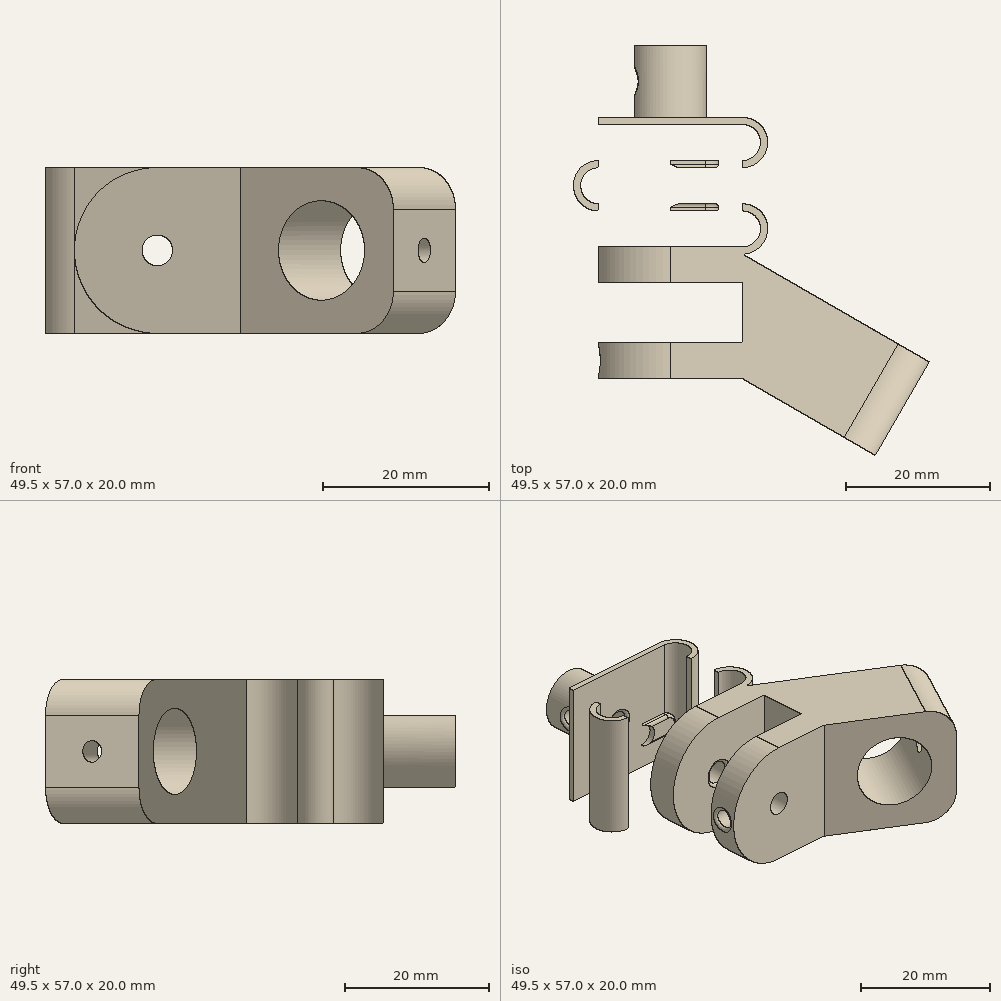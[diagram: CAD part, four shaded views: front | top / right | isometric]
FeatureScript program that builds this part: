
annotation { "Feature Type Name" : "Feature", "Feature Type Description" : "" }
export const myFeature = defineFeature(function(context is Context, id is Id, definition is map)
    precondition{}
    {
        {
            var Q0;
            Q0=qCreatedBy(makeId("Top.planeOp"),FACE);
            var sketch = newSketch(context, id + "F0", { "sketchPlane" : qUnion([Q0])});
            skLineSegment(sketch, "E0", {"start": v(0, 0) * mm, "end": v(25.98, -15) * mm});
            skLineSegment(sketch, "E1", {"start": v(25.98, -15) * mm, "end": v(18.48, -28) * mm});
            skLineSegment(sketch, "E2", {"start": v(18.48, -28) * mm, "end": v(0, -17.32) * mm});
            skLineSegment(sketch, "E3", {"start": v(0, -17.32) * mm, "end": v(0, 0) * mm});
            skLineSegment(sketch, "E4.bottom", {"start": v(0, -4) * mm, "end": v(-20, -4) * mm});
            skLineSegment(sketch, "E4.top", {"start": v(0, 1) * mm, "end": v(-20, 1) * mm});
            skLineSegment(sketch, "E4.left", {"start": v(0, -4) * mm, "end": v(0, 1) * mm});
            skLineSegment(sketch, "E4.right", {"start": v(-20, -4) * mm, "end": v(-20, 1) * mm});
            skLineSegment(sketch, "E5.bottom", {"start": v(0, 6) * mm, "end": v(-20, 6) * mm});
            skLineSegment(sketch, "E5.top", {"start": v(0, 7) * mm, "end": v(-20, 7) * mm});
            skLineSegment(sketch, "E5.left", {"start": v(0, 6) * mm, "end": v(0, 7) * mm});
            skLineSegment(sketch, "E5.right", {"start": v(-20, 6) * mm, "end": v(-20, 7) * mm});
            skLineSegment(sketch, "E6.bottom", {"start": v(0, 12) * mm, "end": v(-20, 12) * mm});
            skLineSegment(sketch, "E6.top", {"start": v(0, 13) * mm, "end": v(-20, 13) * mm});
            skLineSegment(sketch, "E6.left", {"start": v(0, 12) * mm, "end": v(0, 13) * mm});
            skLineSegment(sketch, "E6.right", {"start": v(-20, 12) * mm, "end": v(-20, 13) * mm});
            skLineSegment(sketch, "E7.bottom", {"start": v(0, 18) * mm, "end": v(-20, 18) * mm});
            skLineSegment(sketch, "E7.top", {"start": v(0, 19) * mm, "end": v(-20, 19) * mm});
            skLineSegment(sketch, "E7.left", {"start": v(0, 18) * mm, "end": v(0, 19) * mm});
            skLineSegment(sketch, "E7.right", {"start": v(-20, 18) * mm, "end": v(-20, 19) * mm});
            skLineSegment(sketch, "E8.bottom", {"start": v(0, -17.32) * mm, "end": v(-20, -17.32) * mm});
            skLineSegment(sketch, "E8.top", {"start": v(0, -12.32) * mm, "end": v(-20, -12.32) * mm});
            skLineSegment(sketch, "E8.left", {"start": v(0, -17.32) * mm, "end": v(0, -12.32) * mm});
            skLineSegment(sketch, "E8.right", {"start": v(-20, -17.32) * mm, "end": v(-20, -12.32) * mm});
            skArc(sketch, "E9", {"start": v(0, 6) * mm, "mid": v(2.5, 3.5) * mm, "end": v(0, 1) * mm});
            skArc(sketch, "E10", {"start": v(0, 7) * mm, "mid": v(3.5, 3.5) * mm, "end": v(0, 0) * mm});
            skArc(sketch, "E11", {"start": v(-20, 7) * mm, "mid": v(-22.5, 9.5) * mm, "end": v(-20, 12) * mm});
            skArc(sketch, "E12", {"start": v(-20, 13) * mm, "mid": v(-23.5, 9.5) * mm, "end": v(-20, 6) * mm});
            skArc(sketch, "E13", {"start": v(0, 18) * mm, "mid": v(2.5, 15.5) * mm, "end": v(0, 13) * mm});
            skArc(sketch, "E14", {"start": v(0, 19) * mm, "mid": v(3.5, 15.5) * mm, "end": v(0, 12) * mm});
            skSolve(sketch);
        }
        {
            var Q0;
            Q0 = qSketchRegion(id + "F0", true);
            extrude(context, id + "F1", {"entities" : qUnion([Q0]), "depth" : 20 * mm, "offsetDistance" : 25 * mm});
        }
        {
            var Q0;
            Q0=makeQuery(id+"F1.opExtrude","SWEPT_FACE",FACE,{"disambiguationData":[OSD([sQuery(id+"F0.wireOp",EDGE,"E0")])]});
            var sketch = newSketch(context, id + "F2", { "sketchPlane" : qUnion([Q0])});
            skCircle(sketch, "E15", {"center": v(-20, 10) * mm, "radius": 6 * mm});
            skLineSegment(sketch, "E16", {"start": v(-20, 10) * mm, "end": v(-20, 0) * mm, "construction": true});
            skLineSegment(sketch, "E17", {"start": v(-20, 10) * mm, "end": v(-30, 10) * mm, "construction": true});
            skSolve(sketch);
        }
        {
            var Q0;
            Q0=makeQuery(id+"F2.imprint","IMPRINT",FACE,{"disambiguationData":[TD([[makeQuery(id+"F2.imprint","IMPRINT",EDGE,{"derivedFrom":sQuery(id+"F2.wireOp",EDGE,"E15")}),1.0]])]});
            var Q1;
            Q1=makeQuery(id+"F1.opExtrude","SWEPT_FACE",FACE,{"disambiguationData":[OSD([sQuery(id+"F0.wireOp",EDGE,"E2")])]});
            extrude(context, id + "F3", {"entities" : qUnion([Q0]), "operationType" : NewBodyOperationType.REMOVE, "endBound" : BoundingType.UP_TO_SURFACE, "oppositeDirection" : true, "depth" : 25 * mm, "endBoundEntityFace" : qUnion([Q1]), "offsetDistance" : 25 * mm});
        }
        {
            var Q0;
            Q0=makeQuery(id+"F1.opExtrude","SWEPT_FACE",FACE,{"disambiguationData":[OSD([sQuery(id+"F0.wireOp",EDGE,"E1")])]});
            var sketch = newSketch(context, id + "F4", { "sketchPlane" : qUnion([Q0])});
            skCircle(sketch, "E18", {"center": v(-7.5, 10) * mm, "radius": 1.5 * mm});
            skPoint(sketch, "E19", {"position": v(0, 10) * mm});
            skPoint(sketch, "E20", {"position": v(-7.5, 0) * mm});
            skSolve(sketch);
        }
        {
            var Q0;
            Q0=makeQuery(id+"F4.imprint","IMPRINT",FACE,{"disambiguationData":[TD([[makeQuery(id+"F4.imprint","IMPRINT",EDGE,{"derivedFrom":sQuery(id+"F4.wireOp",EDGE,"E18")}),1.0]])]});
            var Q1;
            Q1=makeQuery(id+"F3.boolean.opBoolean","COPY",FACE,{"derivedFrom":makeQuery(id+"F3.opExtrude","SWEPT_FACE",FACE,{"disambiguationData":[OSD([sQuery(id+"F2.wireOp",EDGE,"E15")])]})});
            extrude(context, id + "F5", {"entities" : qUnion([Q0]), "operationType" : NewBodyOperationType.REMOVE, "endBound" : BoundingType.UP_TO_SURFACE, "oppositeDirection" : true, "depth" : 25 * mm, "endBoundEntityFace" : qUnion([Q1]), "offsetDistance" : 25 * mm});
        }
        {
            var Q0;
            Q0=makeQuery(id+"F1.opExtrude","SWEPT_FACE",FACE,{"disambiguationData":[OSD([sQuery(id+"F0.wireOp",EDGE,"E8.bottom")])]});
            var sketch = newSketch(context, id + "F6", { "sketchPlane" : qUnion([Q0])});
            skCircle(sketch, "E21", {"center": v(-10, 10) * mm, "radius": 1.85 * mm});
            skPoint(sketch, "E22", {"position": v(-20, 10) * mm});
            skPoint(sketch, "E23", {"position": v(-10, 0) * mm});
            skSolve(sketch);
        }
        {
            var Q0;
            Q0=makeQuery(id+"F1.opExtrude","SWEPT_FACE",FACE,{"disambiguationData":[OSD([sQuery(id+"F0.wireOp",EDGE,"E7.top")])]});
            var sketch = newSketch(context, id + "F7", { "sketchPlane" : qUnion([Q0])});
            skLineSegment(sketch, "E24.bottom", {"start": v(15, 5) * mm, "end": v(5, 5) * mm});
            skLineSegment(sketch, "E24.top", {"start": v(15, 15) * mm, "end": v(5, 15) * mm});
            skLineSegment(sketch, "E24.left", {"start": v(15, 5) * mm, "end": v(15, 15) * mm});
            skLineSegment(sketch, "E24.right", {"start": v(5, 5) * mm, "end": v(5, 15) * mm});
            skPoint(sketch, "E25", {"position": v(15, 10) * mm});
            skPoint(sketch, "E26", {"position": v(10, 5) * mm});
            skSolve(sketch);
        }
        {
            var Q0;
            Q0=makeQuery(id+"F7.imprint","IMPRINT",FACE,{"disambiguationData":[TD([[makeQuery(id+"F7.imprint","IMPRINT",EDGE,{"derivedFrom":sQuery(id+"F7.wireOp",EDGE,"E24.bottom")}),-1.0]])]});
            extrude(context, id + "F8", {"entities" : qUnion([Q0]), "operationType" : NewBodyOperationType.ADD, "depth" : 10 * mm, "offsetDistance" : 25 * mm});
        }
        {
            var Q0;
            Q0=makeQuery(id+"F6.imprint","IMPRINT",FACE,{"disambiguationData":[TD([[makeQuery(id+"F6.imprint","IMPRINT",EDGE,{"derivedFrom":sQuery(id+"F6.wireOp",EDGE,"E21")}),1.0]])]});
            var Q1;
            Q1=makeQuery(id+"F8.opExtrude","CAP_FACE",FACE,{"disambiguationData":[OSD([sQuery(id+"F7.wireOp",EDGE,"E24.bottom"),sQuery(id+"F7.wireOp",EDGE,"E24.top"),sQuery(id+"F7.wireOp",EDGE,"E24.left"),sQuery(id+"F7.wireOp",EDGE,"E24.right")])],"isStart":false});
            extrude(context, id + "F9", {"entities" : qUnion([Q0]), "operationType" : NewBodyOperationType.REMOVE, "endBound" : BoundingType.UP_TO_SURFACE, "oppositeDirection" : true, "depth" : 25 * mm, "endBoundEntityFace" : qUnion([Q1]), "offsetDistance" : 25 * mm});
        }
        {
            var Q0;
            Q0=makeQuery(id+"F1.opExtrude","SWEPT_FACE",FACE,{"disambiguationData":[OSD([sQuery(id+"F0.wireOp",EDGE,"E8.right")])]});
            var sketch = newSketch(context, id + "F10", { "sketchPlane" : qUnion([Q0])});
            skCircle(sketch, "E27", {"center": v(14.82, 10) * mm, "radius": 1.5 * mm});
            skPoint(sketch, "E28", {"position": v(14.82, 20) * mm});
            skPoint(sketch, "E29", {"position": v(12.32, 10) * mm});
            skSolve(sketch);
        }
        {
            var Q0;
            Q0=makeQuery(id+"F10.imprint","IMPRINT",FACE,{"disambiguationData":[TD([[makeQuery(id+"F10.imprint","IMPRINT",EDGE,{"derivedFrom":sQuery(id+"F10.wireOp",EDGE,"E27")}),1.0]])]});
            var Q1;
            Q1=sQuery(id+"F10.wireOp",EDGE,"E27");
            var Q2;
            Q2=makeQuery(id+"F9.boolean.opBoolean","COPY",FACE,{"disambiguationData":[TD([makeQuery(id+"F1.opExtrude","SWEPT_FACE",FACE,{"disambiguationData":[OSD([sQuery(id+"F0.wireOp",EDGE,"E8.bottom")])]})])],"derivedFrom":makeQuery(id+"F9.opExtrude","SWEPT_FACE",FACE,{"disambiguationData":[OSD([sQuery(id+"F6.wireOp",EDGE,"E21")])]})});
            extrude(context, id + "F11", {"entities" : qUnion([Q0]), "operationType" : NewBodyOperationType.REMOVE, "surfaceEntities" : qUnion([Q1]), "endBound" : BoundingType.UP_TO_SURFACE, "oppositeDirection" : true, "depth" : 25 * mm, "endBoundEntityFace" : qUnion([Q2]), "offsetDistance" : 25 * mm});
        }
        {
            var Q0;
            Q0=makeQuery(id+"F8.opExtrude","SWEPT_FACE",FACE,{"disambiguationData":[OSD([sQuery(id+"F7.wireOp",EDGE,"E24.left")])]});
            var sketch = newSketch(context, id + "F12", { "sketchPlane" : qUnion([Q0])});
            skCircle(sketch, "E30", {"center": v(-24, 10) * mm, "radius": 1.5 * mm});
            skPoint(sketch, "E31", {"position": v(-24, 15) * mm});
            skPoint(sketch, "E32", {"position": v(-29, 10) * mm});
            skSolve(sketch);
        }
        {
            var Q0;
            Q0=makeQuery(id+"F12.imprint","IMPRINT",FACE,{"disambiguationData":[TD([[makeQuery(id+"F12.imprint","IMPRINT",EDGE,{"derivedFrom":sQuery(id+"F12.wireOp",EDGE,"E30")}),1.0]])]});
            var Q1;
            Q1=makeQuery(id+"F9.boolean.opBoolean","COPY",FACE,{"disambiguationData":[TD([makeQuery(id+"F1.opExtrude","SWEPT_FACE",FACE,{"disambiguationData":[OSD([sQuery(id+"F0.wireOp",EDGE,"E7.bottom")])]})])],"derivedFrom":makeQuery(id+"F9.opExtrude","SWEPT_FACE",FACE,{"disambiguationData":[OSD([sQuery(id+"F6.wireOp",EDGE,"E21")])]})});
            extrude(context, id + "F13", {"entities" : qUnion([Q0]), "operationType" : NewBodyOperationType.REMOVE, "endBound" : BoundingType.UP_TO_SURFACE, "oppositeDirection" : true, "depth" : 25 * mm, "endBoundEntityFace" : qUnion([Q1]), "offsetDistance" : 25 * mm});
        }
        {
            var Q0;
            Q0=makeQuery(id+"F1.opExtrude","SWEPT_FACE",FACE,{"disambiguationData":[OSD([sQuery(id+"F0.wireOp",EDGE,"E5.top")])]});
            var sketch = newSketch(context, id + "F14", { "sketchPlane" : qUnion([Q0])});
            skLineSegment(sketch, "E33.bottom", {"start": v(14.85, 8.15) * mm, "end": v(5.15, 8.15) * mm});
            skLineSegment(sketch, "E33.top", {"start": v(14.85, 11.85) * mm, "end": v(5.15, 11.85) * mm});
            skLineSegment(sketch, "E33.left", {"start": v(14.85, 8.15) * mm, "end": v(14.85, 11.85) * mm, "construction": true});
            skLineSegment(sketch, "E33.right", {"start": v(5.15, 8.15) * mm, "end": v(5.15, 11.85) * mm, "construction": true});
            skPoint(sketch, "E34", {"position": v(10, 11.85) * mm});
            skArc(sketch, "E35", {"start": v(5.15, 8.15) * mm, "mid": v(3.3, 10) * mm, "end": v(5.15, 11.85) * mm});
            skArc(sketch, "E36", {"start": v(14.85, 8.15) * mm, "mid": v(16.7, 10) * mm, "end": v(14.85, 11.85) * mm});
            skSolve(sketch);
        }
        {
            var Q0;
            {var subQ0=sQuery(id+"F14.wireOp",EDGE,"E35");Q0=makeQuery(id+"F14.imprint","IMPRINT",FACE,{"disambiguationData":[TD([[makeQuery(id+"F14.imprint","IMPRINT",EDGE,{"derivedFrom":subQ0}),-1.0]])]});}
            var Q1;
            {var subQ0=sQuery(id+"F14.wireOp",EDGE,"E36");Q1=makeQuery(id+"F14.imprint","IMPRINT",FACE,{"disambiguationData":[TD([[makeQuery(id+"F14.imprint","IMPRINT",EDGE,{"derivedFrom":subQ0}),1.0]])]});}
            var Q2;
            Q2=makeQuery(id+"F1.opExtrude","SWEPT_FACE",FACE,{"disambiguationData":[OSD([sQuery(id+"F0.wireOp",EDGE,"E5.bottom")])]});
            var Q3;
            Q3=makeQuery(id+"F1.opExtrude","SWEPT_FACE",FACE,{"disambiguationData":[OSD([sQuery(id+"F0.wireOp",EDGE,"E6.top")])]});
            extrude(context, id + "F15", {"entities" : qUnion([Q0, Q1]), "operationType" : NewBodyOperationType.REMOVE, "endBound" : BoundingType.UP_TO_SURFACE, "oppositeDirection" : true, "depth" : 4 * mm, "endBoundEntityFace" : qUnion([Q2]), "offsetDistance" : 25 * mm, "hasSecondDirection" : true, "secondDirectionBound" : SecondDirectionBoundingType.UP_TO_SURFACE, "secondDirectionOppositeDirection" : false, "secondDirectionDepth" : 25 * mm, "secondDirectionBoundEntityFace" : qUnion([Q3])});
        }
        {
            var Q0;
            Q0=makeQuery(id+"F1.opExtrude","CAP_EDGE",EDGE,{"disambiguationData":[OSD([sQuery(id+"F0.wireOp",EDGE,"E1")])],"isStart":false});
            var Q1;
            Q1=makeQuery(id+"F1.opExtrude","CAP_EDGE",EDGE,{"disambiguationData":[OSD([sQuery(id+"F0.wireOp",EDGE,"E1")])],"isStart":true});
            var Q2;
            Q2=makeQuery(id+"F8.opExtrude","SWEPT_EDGE",EDGE,{"disambiguationData":[OSD([sQuery(id+"F7.wireOp",EDGE,"E24.top"),sQuery(id+"F7.wireOp",EDGE,"E24.left")])]});
            var Q3;
            Q3=makeQuery(id+"F8.opExtrude","SWEPT_EDGE",EDGE,{"disambiguationData":[OSD([sQuery(id+"F7.wireOp",EDGE,"E24.top"),sQuery(id+"F7.wireOp",EDGE,"E24.right")])]});
            var Q4;
            Q4=makeQuery(id+"F8.opExtrude","SWEPT_EDGE",EDGE,{"disambiguationData":[OSD([sQuery(id+"F7.wireOp",EDGE,"E24.bottom"),sQuery(id+"F7.wireOp",EDGE,"E24.right")])]});
            var Q5;
            Q5=makeQuery(id+"F8.opExtrude","SWEPT_EDGE",EDGE,{"disambiguationData":[OSD([sQuery(id+"F7.wireOp",EDGE,"E24.bottom"),sQuery(id+"F7.wireOp",EDGE,"E24.left")])]});
            fillet(context, id + "F16", {"entities" : qUnion([Q0, Q1, Q2, Q3, Q4, Q5]), "radius" : 5 * mm, "tangentPropagation" : true, "allowEdgeOverflow" : false});
        }
        {
            var Q0;
            Q0=makeQuery(id+"F1.opExtrude","CAP_EDGE",EDGE,{"disambiguationData":[OSD([sQuery(id+"F0.wireOp",EDGE,"E8.right")])],"isStart":false});
            var Q1;
            Q1=makeQuery(id+"F1.opExtrude","CAP_EDGE",EDGE,{"disambiguationData":[OSD([sQuery(id+"F0.wireOp",EDGE,"E8.right")])],"isStart":true});
            var Q2;
            Q2=makeQuery(id+"F1.opExtrude","CAP_EDGE",EDGE,{"disambiguationData":[OSD([sQuery(id+"F0.wireOp",EDGE,"E4.right")])],"isStart":false});
            var Q3;
            Q3=makeQuery(id+"F1.opExtrude","CAP_EDGE",EDGE,{"disambiguationData":[OSD([sQuery(id+"F0.wireOp",EDGE,"E4.right")])],"isStart":true});
            fillet(context, id + "F17", {"entities" : qUnion([Q0, Q1, Q2, Q3]), "radius" : 10 * mm, "tangentPropagation" : true, "allowEdgeOverflow" : false});
        }
        {
            var Q0;
            Q0=makeQuery(id+"F5.boolean.opBoolean","COPY",EDGE,{"derivedFrom":makeQuery(id+"F5.opExtrude","CAP_EDGE",EDGE,{"disambiguationData":[OSD([sQuery(id+"F4.wireOp",EDGE,"E18")])],"isStart":true})});
            var Q1;
            Q1=makeQuery(id+"F9.boolean.opBoolean","COPY",EDGE,{"derivedFrom":makeQuery(id+"F9.opExtrude","TWEAK_EDGE",EDGE,{"derivedFrom":[makeQuery(id+"F6.imprint","IMPRINT",EDGE,{"derivedFrom":sQuery(id+"F6.wireOp",EDGE,"E21")}),makeQuery(id+"F8.opExtrude","CAP_FACE",FACE,{"disambiguationData":[OSD([sQuery(id+"F7.wireOp",EDGE,"E24.bottom"),sQuery(id+"F7.wireOp",EDGE,"E24.top"),sQuery(id+"F7.wireOp",EDGE,"E24.left"),sQuery(id+"F7.wireOp",EDGE,"E24.right")])],"isStart":false})]})});
            var Q2;
            Q2=makeQuery(id+"F13.boolean.opBoolean","COPY",EDGE,{"derivedFrom":makeQuery(id+"F13.opExtrude","CAP_EDGE",EDGE,{"disambiguationData":[OSD([sQuery(id+"F12.wireOp",EDGE,"E30")])],"isStart":true})});
            var Q3;
            Q3=makeQuery(id+"F9.boolean.opBoolean","COPY",EDGE,{"derivedFrom":makeQuery(id+"F9.opExtrude","CAP_EDGE",EDGE,{"disambiguationData":[OSD([sQuery(id+"F6.wireOp",EDGE,"E21")])],"isStart":true})});
            var Q4;
            Q4=makeQuery(id+"F9.boolean.opBoolean","INTERSECT",EDGE,{"derivedFrom":[makeQuery(id+"F1.opExtrude","SWEPT_FACE",FACE,{"disambiguationData":[OSD([sQuery(id+"F0.wireOp",EDGE,"E4.bottom")])]}),makeQuery(id+"F9.opExtrude","SWEPT_FACE",FACE,{"disambiguationData":[OSD([sQuery(id+"F6.wireOp",EDGE,"E21")])]})]});
            var Q5;
            Q5=makeQuery(id+"F9.boolean.opBoolean","INTERSECT",EDGE,{"derivedFrom":[makeQuery(id+"F1.opExtrude","SWEPT_FACE",FACE,{"disambiguationData":[OSD([sQuery(id+"F0.wireOp",EDGE,"E8.top")])]}),makeQuery(id+"F9.opExtrude","SWEPT_FACE",FACE,{"disambiguationData":[OSD([sQuery(id+"F6.wireOp",EDGE,"E21")])]})]});
            var Q6;
            Q6=makeQuery(id+"F9.boolean.opBoolean","INTERSECT",EDGE,{"derivedFrom":[makeQuery(id+"F1.opExtrude","SWEPT_FACE",FACE,{"disambiguationData":[OSD([sQuery(id+"F0.wireOp",EDGE,"E4.top")])]}),makeQuery(id+"F9.opExtrude","SWEPT_FACE",FACE,{"disambiguationData":[OSD([sQuery(id+"F6.wireOp",EDGE,"E21")])]})]});
            var Q7;
            Q7=makeQuery(id+"F9.boolean.opBoolean","INTERSECT",EDGE,{"derivedFrom":[makeQuery(id+"F1.opExtrude","SWEPT_FACE",FACE,{"disambiguationData":[OSD([sQuery(id+"F0.wireOp",EDGE,"E7.bottom")])]}),makeQuery(id+"F9.opExtrude","SWEPT_FACE",FACE,{"disambiguationData":[OSD([sQuery(id+"F6.wireOp",EDGE,"E21")])]})]});
            var Q8;
            Q8=makeQuery(id+"F3.boolean.opBoolean","COPY",EDGE,{"derivedFrom":makeQuery(id+"F3.opExtrude","CAP_EDGE",EDGE,{"disambiguationData":[OSD([sQuery(id+"F2.wireOp",EDGE,"E15")])],"isStart":true})});
            var Q9;
            Q9=makeQuery(id+"F3.boolean.opBoolean","COPY",EDGE,{"derivedFrom":makeQuery(id+"F3.opExtrude","TWEAK_EDGE",EDGE,{"derivedFrom":[makeQuery(id+"F1.opExtrude","SWEPT_FACE",FACE,{"disambiguationData":[OSD([sQuery(id+"F0.wireOp",EDGE,"E2")])]}),makeQuery(id+"F2.imprint","IMPRINT",EDGE,{"derivedFrom":sQuery(id+"F2.wireOp",EDGE,"E15")})]})});
            var Q10;
            {var subQ0=sQuery(id+"F14.wireOp",EDGE,"E33.top");var subQ1=makeQuery(id+"F1.opExtrude","SWEPT_FACE",FACE,{"disambiguationData":[OSD([sQuery(id+"F0.wireOp",EDGE,"E5.top")])]});Q10=makeQuery(id+"F15.boolean.opBoolean","INTERSECT",EDGE,{"derivedFrom":[subQ1,makeQuery(id+"F15.opExtrude","SWEPT_FACE",FACE,{"disambiguationData":[OSD([subQ0]),TDD([makeQuery(id+"F14.imprint","IMPRINT",EDGE,{"disambiguationData":[TD([[makeQuery(id+"F14.imprint","INTERSECT",VERTEX,{"derivedFrom":[subQ0,sQuery(id+"F14.wireOp",EDGE,"E36")]}),-1.0]])],"derivedFrom":subQ0})])]}),makeQuery(id+"F15.opExtrude","SWEPT_FACE",FACE,{"disambiguationData":[OSD([subQ0]),TDD([makeQuery(id+"F14.imprint","IMPRINT",EDGE,{"disambiguationData":[TD([[makeQuery(id+"F14.imprint","INTERSECT",VERTEX,{"derivedFrom":[subQ0,sQuery(id+"F14.wireOp",EDGE,"E35")]}),1.0]])],"derivedFrom":subQ0})])]})]});}
            var Q11;
            {var subQ0=sQuery(id+"F14.wireOp",EDGE,"E33.top");var subQ2=makeQuery(id+"F1.opExtrude","SWEPT_FACE",FACE,{"disambiguationData":[OSD([sQuery(id+"F0.wireOp",EDGE,"E6.top")])]});Q11=makeQuery(id+"F15.boolean.opBoolean","TWEAK_EDGE",EDGE,{"derivedFrom":[makeQuery(id+"F15.opExtrude","TWEAK_EDGE",EDGE,{"derivedFrom":[subQ2,makeQuery(id+"F14.imprint","IMPRINT",EDGE,{"disambiguationData":[TD([[makeQuery(id+"F14.imprint","INTERSECT",VERTEX,{"derivedFrom":[subQ0,sQuery(id+"F14.wireOp",EDGE,"E36")]}),-1.0]])],"derivedFrom":subQ0})]}),makeQuery(id+"F15.opExtrude","TWEAK_EDGE",EDGE,{"derivedFrom":[subQ2,makeQuery(id+"F14.imprint","IMPRINT",EDGE,{"disambiguationData":[TD([[makeQuery(id+"F14.imprint","INTERSECT",VERTEX,{"derivedFrom":[subQ0,sQuery(id+"F14.wireOp",EDGE,"E35")]}),1.0]])],"derivedFrom":subQ0})]})]});}
            var Q12;
            {var subQ0=sQuery(id+"F14.wireOp",EDGE,"E33.top");Q12=makeQuery(id+"F15.boolean.opBoolean","INTERSECT",EDGE,{"derivedFrom":[makeQuery(id+"F1.opExtrude","SWEPT_FACE",FACE,{"disambiguationData":[OSD([sQuery(id+"F0.wireOp",EDGE,"E6.bottom")])]}),makeQuery(id+"F15.opExtrude","SWEPT_FACE",FACE,{"disambiguationData":[OSD([subQ0]),TDD([makeQuery(id+"F14.imprint","IMPRINT",EDGE,{"disambiguationData":[TD([[makeQuery(id+"F14.imprint","INTERSECT",VERTEX,{"derivedFrom":[subQ0,sQuery(id+"F14.wireOp",EDGE,"E36")]}),-1.0]])],"derivedFrom":subQ0})])]}),makeQuery(id+"F15.opExtrude","SWEPT_FACE",FACE,{"disambiguationData":[OSD([subQ0]),TDD([makeQuery(id+"F14.imprint","IMPRINT",EDGE,{"disambiguationData":[TD([[makeQuery(id+"F14.imprint","INTERSECT",VERTEX,{"derivedFrom":[subQ0,sQuery(id+"F14.wireOp",EDGE,"E35")]}),1.0]])],"derivedFrom":subQ0})])]})]});}
            var Q13;
            {var subQ0=sQuery(id+"F14.wireOp",EDGE,"E33.top");var subQ2=makeQuery(id+"F1.opExtrude","SWEPT_FACE",FACE,{"disambiguationData":[OSD([sQuery(id+"F0.wireOp",EDGE,"E5.bottom")])]});Q13=makeQuery(id+"F15.boolean.opBoolean","TWEAK_EDGE",EDGE,{"derivedFrom":[makeQuery(id+"F15.opExtrude","TWEAK_EDGE",EDGE,{"derivedFrom":[subQ2,makeQuery(id+"F14.imprint","IMPRINT",EDGE,{"disambiguationData":[TD([[makeQuery(id+"F14.imprint","INTERSECT",VERTEX,{"derivedFrom":[subQ0,sQuery(id+"F14.wireOp",EDGE,"E36")]}),-1.0]])],"derivedFrom":subQ0})]}),makeQuery(id+"F15.opExtrude","TWEAK_EDGE",EDGE,{"derivedFrom":[subQ2,makeQuery(id+"F14.imprint","IMPRINT",EDGE,{"disambiguationData":[TD([[makeQuery(id+"F14.imprint","INTERSECT",VERTEX,{"derivedFrom":[subQ0,sQuery(id+"F14.wireOp",EDGE,"E35")]}),1.0]])],"derivedFrom":subQ0})]})]});}
            var Q14;
            Q14=makeQuery(id+"F16.opFillet","BLEND_EDGE",EDGE,{"blendedFrom":[makeQuery(id+"F8.opExtrude","SWEPT_EDGE",EDGE,{"disambiguationData":[OSD([sQuery(id+"F7.wireOp",EDGE,"E24.bottom"),sQuery(id+"F7.wireOp",EDGE,"E24.right")])]}),makeQuery(id+"F13.boolean.opBoolean","COPY",FACE,{"derivedFrom":makeQuery(id+"F13.opExtrude","SWEPT_FACE",FACE,{"disambiguationData":[OSD([sQuery(id+"F12.wireOp",EDGE,"E30")])]})})],"blendedInto":[makeQuery(id+"F13.boolean.opBoolean","COPY",FACE,{"derivedFrom":makeQuery(id+"F13.opExtrude","SWEPT_FACE",FACE,{"disambiguationData":[OSD([sQuery(id+"F12.wireOp",EDGE,"E30")])]})})]});
            var Q15;
            Q15=makeQuery(id+"F13.boolean.opBoolean","COPY",EDGE,{"derivedFrom":makeQuery(id+"F13.opExtrude","CAP_EDGE",EDGE,{"disambiguationData":[OSD([sQuery(id+"F12.wireOp",EDGE,"E30")])],"isStart":false})});
            var Q16;
            Q16=makeQuery(id+"F5.boolean.opBoolean","COPY",EDGE,{"derivedFrom":makeQuery(id+"F5.opExtrude","TWEAK_EDGE",EDGE,{"derivedFrom":[makeQuery(id+"F3.boolean.opBoolean","COPY",FACE,{"derivedFrom":makeQuery(id+"F3.opExtrude","SWEPT_FACE",FACE,{"disambiguationData":[OSD([sQuery(id+"F2.wireOp",EDGE,"E15")])]})}),makeQuery(id+"F4.imprint","IMPRINT",EDGE,{"derivedFrom":sQuery(id+"F4.wireOp",EDGE,"E18")})]})});
            var Q17;
            Q17=makeQuery(id+"F13.boolean.opBoolean","COPY",FACE,{"derivedFrom":makeQuery(id+"F13.opExtrude","SWEPT_FACE",FACE,{"disambiguationData":[OSD([sQuery(id+"F12.wireOp",EDGE,"E30")])]})});
            var Q18;
            Q18=makeQuery(id+"F11.boolean.opBoolean","COPY",FACE,{"derivedFrom":makeQuery(id+"F11.opExtrude","SWEPT_FACE",FACE,{"disambiguationData":[OSD([sQuery(id+"F10.wireOp",EDGE,"E27")])]})});
            fillet(context, id + "F18", {"entities" : qUnion([Q0, Q1, Q2, Q3, Q4, Q5, Q6, Q7, Q8, Q9, Q10, Q11, Q12, Q13, Q14, Q15, Q16, Q17, Q18]), "radius" : 0.5 * mm, "tangentPropagation" : true, "allowEdgeOverflow" : false});
        }
    });
